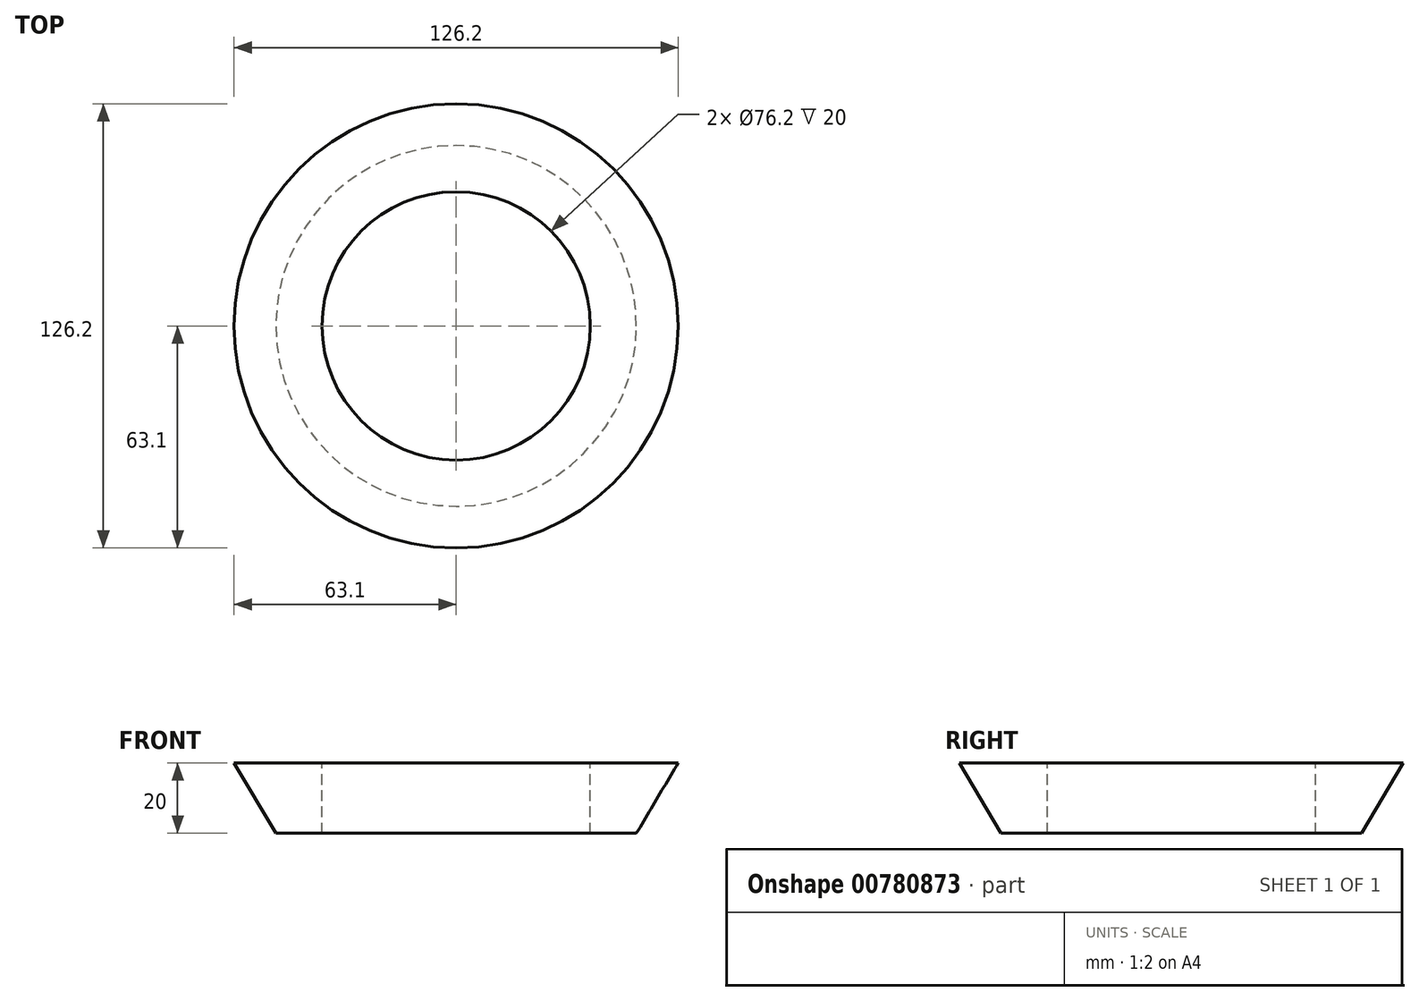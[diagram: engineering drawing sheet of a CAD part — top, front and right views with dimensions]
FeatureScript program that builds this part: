
annotation { "Feature Type Name" : "Feature", "Feature Type Description" : "" }
export const myFeature = defineFeature(function(context is Context, id is Id, definition is map)
    precondition{}
    {
        {
            var Q0;
            Q0=qCreatedBy(makeId("Front.planeOp"),FACE);
            var sketch = newSketch(context, id + "F0", { "sketchPlane" : qUnion([Q0])});
            skLineSegment(sketch, "E0", {"start": v(38.1, 0) * mm, "end": v(38.1, -20) * mm});
            skLineSegment(sketch, "E1", {"start": v(38.1, -20) * mm, "end": v(51.22, -20) * mm});
            skLineSegment(sketch, "E2", {"start": v(51.22, -20) * mm, "end": v(63.1, 0) * mm});
            skLineSegment(sketch, "E3", {"start": v(63.1, 0) * mm, "end": v(38.1, 0) * mm});
            skLineSegment(sketch, "E4", {"start": v(0, 0) * mm, "end": v(0, -12.62) * mm});
            skSolve(sketch);
        }
        {
            var Q0;
            Q0=makeQuery(id+"F0.imprint","IMPRINT",FACE,{"disambiguationData":[TD([[makeQuery(id+"F0.imprint","IMPRINT",EDGE,{"derivedFrom":sQuery(id+"F0.wireOp",EDGE,"E0")}),1.0]])]});
            var Q1;
            Q1=sQuery(id+"F0.wireOp",EDGE,"E4");
            revolve(context, id + "F1", {"surfaceOperationType" : NewSurfaceOperationType.NEW, "entities" : qUnion([Q0]), "axis" : qUnion([Q1]), "revolveType" : RevolveType.FULL});
        }
    });
